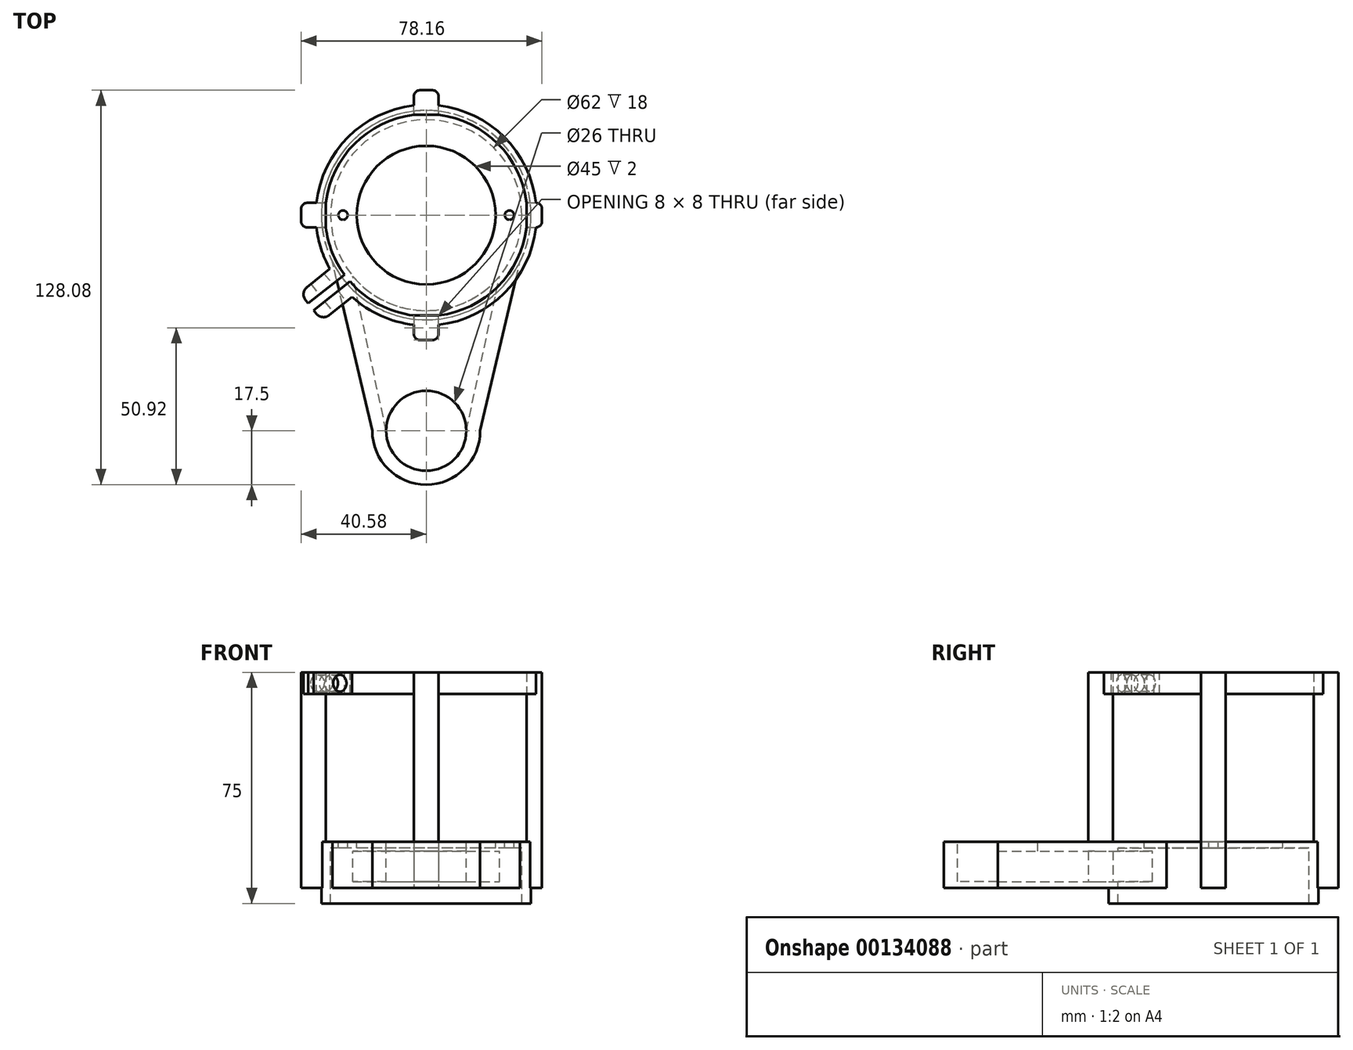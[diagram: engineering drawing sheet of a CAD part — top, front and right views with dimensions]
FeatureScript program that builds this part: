
annotation { "Feature Type Name" : "Feature", "Feature Type Description" : "" }
export const myFeature = defineFeature(function(context is Context, id is Id, definition is map)
    precondition{}
    {
        {
            var Q0;
            Q0=qCreatedBy(makeId("Top.planeOp"),FACE);
            var sketch = newSketch(context, id + "F0", { "sketchPlane" : qUnion([Q0])});
            skCircle(sketch, "E0", {"center": v(0, 0) * mm, "radius": 34 * mm});
            skLineSegment(sketch, "E1", {"start": v(0, 0) * mm, "end": v(0, -70) * mm, "construction": true});
            skCircle(sketch, "E2", {"center": v(0, -70) * mm, "radius": 17.5 * mm});
            skLineSegment(sketch, "E3", {"start": v(-34, 0) * mm, "end": v(34, 0) * mm, "construction": true});
            skLineSegment(sketch, "E4", {"start": v(-17.5, -70) * mm, "end": v(17.5, -70) * mm, "construction": true});
            skLineSegment(sketch, "E5", {"start": v(17.5, -70) * mm, "end": v(34, 0) * mm});
            skLineSegment(sketch, "E6", {"start": v(-17.5, -70) * mm, "end": v(-34, 0) * mm});
            skSolve(sketch);
        }
        {
            var Q0;
            Q0 = qSketchRegion(id + "F0", true);
            extrude(context, id + "F1", {"entities" : qUnion([Q0]), "depth" : 15 * mm});
        }
        {
            var Q0;
            Q0=makeQuery(id+"F1.opExtrude","CAP_FACE",FACE,{"disambiguationData":[OSD([sQuery(id+"F0.wireOp",EDGE,"E0"),sQuery(id+"F0.wireOp",EDGE,"E2"),sQuery(id+"F0.wireOp",EDGE,"E5"),sQuery(id+"F0.wireOp",EDGE,"E6")])],"isStart":false});
            var sketch = newSketch(context, id + "F2", { "sketchPlane" : qUnion([Q0])});
            skCircle(sketch, "E7", {"center": v(0, 0) * mm, "radius": 31 * mm});
            skLineSegment(sketch, "E8", {"start": v(-23.52, -20.2) * mm, "end": v(23.52, -20.2) * mm, "construction": true});
            skSolve(sketch);
        }
        {
            var Q0;
            Q0 = qSketchRegion(id + "F2", true);
            extrude(context, id + "F3", {"entities" : qUnion([Q0]), "operationType" : NewBodyOperationType.REMOVE, "oppositeDirection" : true, "depth" : 21.9 * mm, "hasSecondDirection" : true, "secondDirectionOppositeDirection" : true, "secondDirectionDepth" : 2 * mm});
        }
        {
            var Q0;
            Q0=makeQuery(id+"F1.opExtrude","CAP_FACE",FACE,{"disambiguationData":[OSD([sQuery(id+"F0.wireOp",EDGE,"E0"),sQuery(id+"F0.wireOp",EDGE,"E2"),sQuery(id+"F0.wireOp",EDGE,"E5"),sQuery(id+"F0.wireOp",EDGE,"E6")])],"isStart":false});
            var sketch = newSketch(context, id + "F4", { "sketchPlane" : qUnion([Q0])});
            skCircle(sketch, "E9", {"center": v(0, -70) * mm, "radius": 13 * mm});
            skCircle(sketch, "E10", {"center": v(0, 0) * mm, "radius": 31 * mm});
            skLineSegment(sketch, "E11", {"start": v(-23.86, -19.8) * mm, "end": v(23.86, -19.8) * mm, "construction": true});
            skLineSegment(sketch, "E12", {"start": v(-13, -70) * mm, "end": v(13, -70) * mm, "construction": true});
            skLineSegment(sketch, "E13", {"start": v(-13, -70) * mm, "end": v(-23.86, -19.8) * mm});
            skLineSegment(sketch, "E14", {"start": v(13, -70) * mm, "end": v(23.86, -19.8) * mm});
            skSolve(sketch);
        }
        {
            var Q0;
            Q0 = qSketchRegion(id + "F4", true);
            extrude(context, id + "F5", {"entities" : qUnion([Q0]), "operationType" : NewBodyOperationType.REMOVE, "oppositeDirection" : true, "depth" : 13 * mm, "hasSecondDirection" : true, "secondDirectionOppositeDirection" : true, "secondDirectionDepth" : 3 * mm});
        }
        {
            var Q0;
            Q0=makeQuery(id+"F1.opExtrude","CAP_FACE",FACE,{"disambiguationData":[OSD([sQuery(id+"F0.wireOp",EDGE,"E0"),sQuery(id+"F0.wireOp",EDGE,"E2"),sQuery(id+"F0.wireOp",EDGE,"E5"),sQuery(id+"F0.wireOp",EDGE,"E6")])],"isStart":false});
            var sketch = newSketch(context, id + "F6", { "sketchPlane" : qUnion([Q0])});
            skCircle(sketch, "E15", {"center": v(0, 0) * mm, "radius": 22.5 * mm});
            skCircle(sketch, "E16", {"center": v(0, -70) * mm, "radius": 13 * mm});
            skSolve(sketch);
        }
        {
            var Q0;
            Q0 = qSketchRegion(id + "F6", true);
            extrude(context, id + "F7", {"entities" : qUnion([Q0]), "operationType" : NewBodyOperationType.REMOVE, "oppositeDirection" : true, "depth" : 5 * mm});
        }
        {
            var Q0;
            Q0=qCreatedBy(makeId("Right.planeOp"),FACE);
            var sketch = newSketch(context, id + "F8", { "sketchPlane" : qUnion([Q0])});
            skLineSegment(sketch, "E17", {"start": v(-70, 15) * mm, "end": v(-70, 39.6) * mm, "construction": true});
            skLineSegment(sketch, "E18", {"start": v(-84.42, 15) * mm, "end": v(-85.5, 39.58) * mm});
            skLineSegment(sketch, "E19", {"start": v(0, 15) * mm, "end": v(-81.48, 15) * mm, "construction": true});
            skLineSegment(sketch, "E20", {"start": v(-85.5, 39.58) * mm, "end": v(-87.5, 39.6) * mm});
            skLineSegment(sketch, "E21", {"start": v(-87.5, 15) * mm, "end": v(-87.5, 39.6) * mm});
            skLineSegment(sketch, "E22", {"start": v(-85.5, 39.58) * mm, "end": v(-70, 39.6) * mm, "construction": true});
            skSolve(sketch);
        }
        {
            var Q0;
            Q0 = qSketchRegion(id + "F8", true);
            var Q1;
            Q1=sQuery(id+"F8.wireOp",EDGE,"E21");
            var Q2;
            Q2=sQuery(id+"F8.wireOp",EDGE,"E20");
            var Q3;
            Q3=sQuery(id+"F8.wireOp",EDGE,"E18");
            var Q4;
            Q4=sQuery(id+"F8.wireOp",EDGE,"E17");
            revolve(context, id + "F9", {"bodyType" : ToolBodyType.SURFACE, "operationType" : NewBodyOperationType.ADD, "entities" : qUnion([Q0]), "surfaceEntities" : qUnion([Q1, Q2, Q3]), "axis" : qUnion([Q4]), "revolveType" : RevolveType.FULL});
        }
        {
            var Q0;
            Q0=makeQuery(id+"F1.opExtrude","CAP_FACE",FACE,{"disambiguationData":[OSD([sQuery(id+"F0.wireOp",EDGE,"E0"),sQuery(id+"F0.wireOp",EDGE,"E2"),sQuery(id+"F0.wireOp",EDGE,"E5"),sQuery(id+"F0.wireOp",EDGE,"E6")])],"isStart":true});
            var sketch = newSketch(context, id + "F10", { "sketchPlane" : qUnion([Q0])});
            skCircle(sketch, "E23", {"center": v(0, 0) * mm, "radius": 34 * mm});
            skCircle(sketch, "E24", {"center": v(0, 0) * mm, "radius": 31 * mm});
            skSolve(sketch);
        }
        {
            var Q0;
            Q0 = qSketchRegion(id + "F10", true);
            extrude(context, id + "F11", {"entities" : qUnion([Q0]), "operationType" : NewBodyOperationType.ADD, "depth" : 5 * mm});
        }
        {
            var Q0;
            Q0=makeQuery(id+"F2.imprint","IMPRINT",FACE,{"disambiguationData":[TD([[makeQuery(id+"F2.imprint","IMPRINT",EDGE,{"derivedFrom":sQuery(id+"F2.wireOp",EDGE,"E7")}),-1.0]])]});
            var sketch = newSketch(context, id + "F12", { "sketchPlane" : qUnion([Q0])});
            skLineSegment(sketch, "E25", {"start": v(-27, 0) * mm, "end": v(0, 0) * mm, "construction": true});
            skLineSegment(sketch, "E26", {"start": v(0, 0) * mm, "end": v(27, 0) * mm, "construction": true});
            skCircle(sketch, "E27", {"center": v(-27, 0) * mm, "radius": 1.5 * mm});
            skCircle(sketch, "E28", {"center": v(27, 0) * mm, "radius": 1.5 * mm});
            skSolve(sketch);
        }
        {
            var Q0;
            Q0 = qSketchRegion(id + "F12", true);
            extrude(context, id + "F13", {"entities" : qUnion([Q0]), "operationType" : NewBodyOperationType.REMOVE, "oppositeDirection" : true, "depth" : 5 * mm});
        }
        {
            var Q0;
            Q0=qCreatedBy(makeId("Top.planeOp"),FACE);
            var sketch = newSketch(context, id + "F14", { "sketchPlane" : qUnion([Q0])});
            skCircle(sketch, "E29", {"center": v(0, 0) * mm, "radius": 32.83 * mm, "construction": true});
            skLineSegment(sketch, "E30.bottom", {"start": v(-38.58, -4) * mm, "end": v(-32.58, -4) * mm});
            skLineSegment(sketch, "E30.top", {"start": v(-38.58, 4) * mm, "end": v(-32.58, 4) * mm});
            skLineSegment(sketch, "E30.left", {"start": v(-40.58, -2) * mm, "end": v(-40.58, 2) * mm});
            skLineSegment(sketch, "E30.right", {"start": v(-32.58, -4) * mm, "end": v(-32.58, 4) * mm});
            skLineSegment(sketch, "E31", {"start": v(-36.58, -4) * mm, "end": v(-36.58, 0) * mm, "construction": true});
            skLineSegment(sketch, "E32", {"start": v(-36.58, 0) * mm, "end": v(-36.58, 4) * mm, "construction": true});
            skLineSegment(sketch, "E33.bottom", {"start": v(-4, 32.58) * mm, "end": v(4, 32.58) * mm});
            skLineSegment(sketch, "E33.top", {"start": v(-2, 40.58) * mm, "end": v(2, 40.58) * mm});
            skLineSegment(sketch, "E33.left", {"start": v(-4, 32.58) * mm, "end": v(-4, 38.58) * mm});
            skLineSegment(sketch, "E33.right", {"start": v(4, 32.58) * mm, "end": v(4, 38.58) * mm});
            skLineSegment(sketch, "E34", {"start": v(-4, 36.58) * mm, "end": v(0, 36.58) * mm, "construction": true});
            skLineSegment(sketch, "E35", {"start": v(0, 36.58) * mm, "end": v(4, 36.58) * mm, "construction": true});
            skLineSegment(sketch, "E36.bottom", {"start": v(32.58, -4) * mm, "end": v(35.58, -4) * mm});
            skLineSegment(sketch, "E36.top", {"start": v(32.58, 4) * mm, "end": v(35.58, 4) * mm});
            skLineSegment(sketch, "E36.left", {"start": v(32.58, -4) * mm, "end": v(32.58, 4) * mm});
            skLineSegment(sketch, "E36.right", {"start": v(37.58, -2) * mm, "end": v(37.58, 2) * mm});
            skLineSegment(sketch, "E37", {"start": v(35.08, -4) * mm, "end": v(35.08, 0) * mm, "construction": true});
            skLineSegment(sketch, "E38", {"start": v(35.08, 0) * mm, "end": v(35.08, 4) * mm, "construction": true});
            skPoint(sketch, "E39.visualSharp", {"position": v(-40.58, -4) * mm});
            skArc(sketch, "E39.filletArc", {"start": v(-40.58, -2) * mm, "mid": v(-40, -3.41) * mm, "end": v(-38.58, -4) * mm});
            skPoint(sketch, "E40.visualSharp", {"position": v(-40.58, 4) * mm});
            skArc(sketch, "E40.filletArc", {"start": v(-38.58, 4) * mm, "mid": v(-40, 3.41) * mm, "end": v(-40.58, 2) * mm});
            skPoint(sketch, "E41.visualSharp", {"position": v(-4, 40.58) * mm});
            skArc(sketch, "E41.filletArc", {"start": v(-2, 40.58) * mm, "mid": v(-3.41, 40) * mm, "end": v(-4, 38.58) * mm});
            skPoint(sketch, "E42.visualSharp", {"position": v(4, 40.58) * mm});
            skArc(sketch, "E42.filletArc", {"start": v(4, 38.58) * mm, "mid": v(3.41, 40) * mm, "end": v(2, 40.58) * mm});
            skPoint(sketch, "E43.visualSharp", {"position": v(37.58, -4) * mm});
            skArc(sketch, "E43.filletArc", {"start": v(35.58, -4) * mm, "mid": v(37, -3.41) * mm, "end": v(37.58, -2) * mm});
            skPoint(sketch, "E44.visualSharp", {"position": v(37.58, 4) * mm});
            skArc(sketch, "E44.filletArc", {"start": v(37.58, 2) * mm, "mid": v(37, 3.41) * mm, "end": v(35.58, 4) * mm});
            skLineSegment(sketch, "E45.bottom", {"start": v(-4, -32.58) * mm, "end": v(4, -32.58) * mm});
            skLineSegment(sketch, "E45.top", {"start": v(-2, -40.58) * mm, "end": v(2, -40.58) * mm});
            skLineSegment(sketch, "E45.left", {"start": v(-4, -32.58) * mm, "end": v(-4, -38.58) * mm});
            skLineSegment(sketch, "E45.right", {"start": v(4, -32.58) * mm, "end": v(4, -38.58) * mm});
            skLineSegment(sketch, "E46", {"start": v(-4, -36.58) * mm, "end": v(0, -36.58) * mm, "construction": true});
            skLineSegment(sketch, "E47", {"start": v(0, -36.58) * mm, "end": v(4, -36.58) * mm, "construction": true});
            skPoint(sketch, "E48.visualSharp", {"position": v(-4, -40.58) * mm});
            skArc(sketch, "E48.filletArc", {"start": v(-4, -38.58) * mm, "mid": v(-3.41, -40) * mm, "end": v(-2, -40.58) * mm});
            skPoint(sketch, "E49.visualSharp", {"position": v(4, -40.58) * mm});
            skArc(sketch, "E49.filletArc", {"start": v(2, -40.58) * mm, "mid": v(3.41, -40) * mm, "end": v(4, -38.58) * mm});
            skSolve(sketch);
        }
        {
            var Q0;
            Q0 = qSketchRegion(id + "F14", true);
            extrude(context, id + "F15", {"entities" : qUnion([Q0]), "operationType" : NewBodyOperationType.ADD, "depth" : 70 * mm});
        }
        {
            var Q0;
            Q0=makeQuery(id+"F15.opExtrude","CAP_FACE",FACE,{"disambiguationData":[OSD([sQuery(id+"F14.wireOp",EDGE,"E33.bottom"),sQuery(id+"F14.wireOp",EDGE,"E33.top"),sQuery(id+"F14.wireOp",EDGE,"E33.left"),sQuery(id+"F14.wireOp",EDGE,"E33.right"),sQuery(id+"F14.wireOp",EDGE,"E41.filletArc"),sQuery(id+"F14.wireOp",EDGE,"E42.filletArc")])],"isStart":false});
            var sketch = newSketch(context, id + "F16", { "sketchPlane" : qUnion([Q0])});
            skCircle(sketch, "E50", {"center": v(0, 0) * mm, "radius": 32.83 * mm});
            skCircle(sketch, "E51", {"center": v(0, 0) * mm, "radius": 35.83 * mm});
            skLineSegment(sketch, "E52", {"start": v(32.83, 0) * mm, "end": v(35.83, 0) * mm, "construction": true});
            skSolve(sketch);
        }
        {
            var Q0;
            Q0 = qSketchRegion(id + "F16", true);
            extrude(context, id + "F17", {"entities" : qUnion([Q0]), "operationType" : NewBodyOperationType.ADD, "oppositeDirection" : true, "depth" : 7 * mm});
        }
        {
            var Q0;
            Q0=makeQuery(id+"F17.boolean.opBoolean","MERGE",FACE,{"derivedFrom":[makeQuery(id+"F15.opExtrude","CAP_FACE",FACE,{"disambiguationData":[OSD([sQuery(id+"F14.wireOp",EDGE,"E30.bottom"),sQuery(id+"F14.wireOp",EDGE,"E30.top"),sQuery(id+"F14.wireOp",EDGE,"E30.left"),sQuery(id+"F14.wireOp",EDGE,"E30.right"),sQuery(id+"F14.wireOp",EDGE,"E39.filletArc"),sQuery(id+"F14.wireOp",EDGE,"E40.filletArc")])],"isStart":false}),makeQuery(id+"F15.opExtrude","CAP_FACE",FACE,{"disambiguationData":[OSD([sQuery(id+"F14.wireOp",EDGE,"E33.bottom"),sQuery(id+"F14.wireOp",EDGE,"E33.top"),sQuery(id+"F14.wireOp",EDGE,"E33.left"),sQuery(id+"F14.wireOp",EDGE,"E33.right"),sQuery(id+"F14.wireOp",EDGE,"E41.filletArc"),sQuery(id+"F14.wireOp",EDGE,"E42.filletArc")])],"isStart":false}),makeQuery(id+"F15.opExtrude","CAP_FACE",FACE,{"disambiguationData":[OSD([sQuery(id+"F14.wireOp",EDGE,"E36.bottom"),sQuery(id+"F14.wireOp",EDGE,"E36.top"),sQuery(id+"F14.wireOp",EDGE,"E36.left"),sQuery(id+"F14.wireOp",EDGE,"E36.right"),sQuery(id+"F14.wireOp",EDGE,"E43.filletArc"),sQuery(id+"F14.wireOp",EDGE,"E44.filletArc")])],"isStart":false}),makeQuery(id+"F17.opExtrude","CAP_FACE",FACE,{"disambiguationData":[OSD([sQuery(id+"F16.wireOp",EDGE,"E50"),sQuery(id+"F16.wireOp",EDGE,"E51")])],"isStart":true})]});
            var sketch = newSketch(context, id + "F18", { "sketchPlane" : qUnion([Q0])});
            skLineSegment(sketch, "E53", {"start": v(-31.63, -23.36) * mm, "end": v(-23.33, -16.75) * mm});
            skLineSegment(sketch, "E54", {"start": v(-23.33, -16.75) * mm, "end": v(-21.55, -18.98) * mm});
            skLineSegment(sketch, "E55", {"start": v(-21.55, -18.98) * mm, "end": v(-29.85, -25.6) * mm});
            skLineSegment(sketch, "E56", {"start": v(-29.85, -25.6) * mm, "end": v(-31.63, -23.36) * mm});
            skLineSegment(sketch, "E57", {"start": v(-23.33, -16.75) * mm, "end": v(-26.54, -19.31) * mm, "construction": true});
            skLineSegment(sketch, "E58", {"start": v(-21.55, -18.98) * mm, "end": v(-24.77, -21.54) * mm, "construction": true});
            skSolve(sketch);
        }
        {
            var Q0;
            Q0 = qSketchRegion(id + "F18", true);
            extrude(context, id + "F19", {"entities" : qUnion([Q0]), "operationType" : NewBodyOperationType.REMOVE, "oppositeDirection" : true, "depth" : 9.7 * mm});
        }
        {
            var Q0;
            Q0=makeQuery(id+"F17.boolean.opBoolean","MERGE",FACE,{"derivedFrom":[makeQuery(id+"F15.opExtrude","CAP_FACE",FACE,{"disambiguationData":[OSD([sQuery(id+"F14.wireOp",EDGE,"E30.bottom"),sQuery(id+"F14.wireOp",EDGE,"E30.top"),sQuery(id+"F14.wireOp",EDGE,"E30.left"),sQuery(id+"F14.wireOp",EDGE,"E30.right"),sQuery(id+"F14.wireOp",EDGE,"E39.filletArc"),sQuery(id+"F14.wireOp",EDGE,"E40.filletArc")])],"isStart":false}),makeQuery(id+"F15.opExtrude","CAP_FACE",FACE,{"disambiguationData":[OSD([sQuery(id+"F14.wireOp",EDGE,"E33.bottom"),sQuery(id+"F14.wireOp",EDGE,"E33.top"),sQuery(id+"F14.wireOp",EDGE,"E33.left"),sQuery(id+"F14.wireOp",EDGE,"E33.right"),sQuery(id+"F14.wireOp",EDGE,"E41.filletArc"),sQuery(id+"F14.wireOp",EDGE,"E42.filletArc")])],"isStart":false}),makeQuery(id+"F15.opExtrude","CAP_FACE",FACE,{"disambiguationData":[OSD([sQuery(id+"F14.wireOp",EDGE,"E36.bottom"),sQuery(id+"F14.wireOp",EDGE,"E36.top"),sQuery(id+"F14.wireOp",EDGE,"E36.left"),sQuery(id+"F14.wireOp",EDGE,"E36.right"),sQuery(id+"F14.wireOp",EDGE,"E43.filletArc"),sQuery(id+"F14.wireOp",EDGE,"E44.filletArc")])],"isStart":false}),makeQuery(id+"F17.opExtrude","CAP_FACE",FACE,{"disambiguationData":[OSD([sQuery(id+"F16.wireOp",EDGE,"E50"),sQuery(id+"F16.wireOp",EDGE,"E51")])],"isStart":true})]});
            var sketch = newSketch(context, id + "F20", { "sketchPlane" : qUnion([Q0])});
            skLineSegment(sketch, "E59", {"start": v(-26.54, -19.31) * mm, "end": v(-29.29, -15.86) * mm});
            skLineSegment(sketch, "E60", {"start": v(-29.29, -15.86) * mm, "end": v(-38.68, -23.34) * mm});
            skLineSegment(sketch, "E61", {"start": v(-39.16, -27.55) * mm, "end": v(-38.28, -28.65) * mm});
            skLineSegment(sketch, "E62", {"start": v(-38.28, -28.65) * mm, "end": v(-26.54, -19.31) * mm});
            skLineSegment(sketch, "E63", {"start": v(-24.77, -21.54) * mm, "end": v(-36.5, -30.89) * mm});
            skLineSegment(sketch, "E64", {"start": v(-36.5, -30.89) * mm, "end": v(-35.62, -31.99) * mm});
            skLineSegment(sketch, "E65", {"start": v(-31.4, -32.47) * mm, "end": v(-22.02, -25) * mm});
            skLineSegment(sketch, "E66", {"start": v(-22.02, -25) * mm, "end": v(-24.77, -21.54) * mm});
            skPoint(sketch, "E67.visualSharp", {"position": v(-33.75, -34.34) * mm});
            skArc(sketch, "E67.filletArc", {"start": v(-35.62, -31.99) * mm, "mid": v(-33.61, -33.1) * mm, "end": v(-31.4, -32.47) * mm});
            skPoint(sketch, "E68.visualSharp", {"position": v(-41.02, -25.2) * mm});
            skArc(sketch, "E68.filletArc", {"start": v(-38.68, -23.34) * mm, "mid": v(-39.79, -25.35) * mm, "end": v(-39.16, -27.55) * mm});
            skSolve(sketch);
        }
        {
            var Q0;
            Q0 = qSketchRegion(id + "F20", true);
            extrude(context, id + "F21", {"entities" : qUnion([Q0]), "operationType" : NewBodyOperationType.ADD, "oppositeDirection" : true, "depth" : 7 * mm});
        }
        {
            var Q0;
            Q0=makeQuery(id+"F21.opExtrude","SWEPT_FACE",FACE,{"disambiguationData":[OSD([sQuery(id+"F20.wireOp",EDGE,"E65")])]});
            var sketch = newSketch(context, id + "F22", { "sketchPlane" : qUnion([Q0])});
            skLineSegment(sketch, "E69", {"start": v(-40.47, 70) * mm, "end": v(-40.47, 66.5) * mm, "construction": true});
            skLineSegment(sketch, "E70", {"start": v(-40.47, 66.5) * mm, "end": v(-40.47, 63) * mm, "construction": true});
            skLineSegment(sketch, "E71", {"start": v(-44.8, 66.5) * mm, "end": v(-40.47, 66.5) * mm, "construction": true});
            skLineSegment(sketch, "E72", {"start": v(-40.47, 66.5) * mm, "end": v(-35.35, 66.5) * mm, "construction": true});
            skCircle(sketch, "E73", {"center": v(-40.47, 66.5) * mm, "radius": 2.75 * mm});
            skSolve(sketch);
        }
        {
            var Q0;
            Q0 = qSketchRegion(id + "F22", true);
            extrude(context, id + "F23", {"entities" : qUnion([Q0]), "operationType" : NewBodyOperationType.REMOVE, "oppositeDirection" : true, "depth" : 14.84 * mm});
        }
    });
